# Revit family: Thorn PUNCH 3
name_source: partatom
category: Lighting Fixtures
revit_build: Autodesk Revit 2016 (Build: 20150220_1215(x64)
units: mm (PartAtom-declared; Revit-internal decimal feet)

## family parameters
Cut with Voids When Loaded = No
Host = Face
Light Source = Yes
OmniClass Number = 23.80.70.11
OmniClass Title = Luminaries for Internal Lighting
Part Type = Normal
Room Calculation Point = No
Round Connector Dimension = Use Diameter
Shared = No

## types (6) — shared parameters
Assembly Code = D5020200
Body = ZG_Metal_White
Color Filter = 16777215
Cover = ZG_PMMA_Opaque
Description = Surface mount or pendant LED luminaire
Dimming Lamp Color Temperature Shift = <None>
Emit Shape Visible in Rendering = No
Emit from Rectangle Length = 75 mm
Lamp = LED
Manufacturer = Thorn Lighting
Tilt Angle = -90.00°
URL = http://www.thornlighting.com
Voltage = 230 V
Width = 162 mm  [stored 0.531496 ft]
zero-valued in all types: Default Elevation

## per-type parameters (varying)
| type | Apparent Load | Emit from Rectangle Width | Height | Length | Length 1200 | Length 1500 | Model | Photometric Web File | Surface Mount |
| PUNCH 3 4000 L1200 | 35 VA | 1160 mm  [stored 3.80577 ft] | 44 mm  [stored 0.144357 ft] | 1210 mm  [stored 3.96982 ft] | Yes | No | 96630507 | 96630507_(STD).IES | Yes |
| PUNCH 3 6000 L1500 | 52 VA | 1440 mm  [stored 4.72441 ft] | 44 mm  [stored 0.144357 ft] | 1490 mm  [stored 4.88845 ft] | No | Yes | 96667223 | 96667223_(STD).IES | Yes |
| PUNCH 3 ASYM 2200 L1200 | 16 VA | 1130 mm  [stored 3.70735 ft] | 50 mm  [stored 0.164042 ft] | 1180 mm  [stored 3.87139 ft] | Yes | No | 96630503 | 96630503_(STD).IES | No |
| PUNCH 3 D 4000 L1200 | 35 VA | 1152 mm  [stored 3.77953 ft] | 50 mm  [stored 0.164042 ft] | 1202 mm  [stored 3.94357 ft] | Yes | No | 96667211 | 96667211_(STD).IES | No |
| PUNCH 3 DI 5500 L1200 | 46 VA | 1152 mm  [stored 3.77953 ft] | 50 mm  [stored 0.164042 ft] | 1202 mm  [stored 3.94357 ft] | Yes | No | 96630505 | 96630505_(STD).IES | No |
| PUNCH 3 DI 6600 L1500 | 52 VA | 1432 mm  [stored 4.69816 ft] | 50 mm  [stored 0.164042 ft] | 1482 mm  [stored 4.8622 ft] | No | Yes | 96667218 | 96667218_(STD).IES | No |

note: [stored X ft] marks values corroborated as IEEE doubles in the binary element streams (Revit-internal decimal feet)

## geometry (parser evidence)
native form markers: Sweep x5
no freeform markers — native parametric forms only
